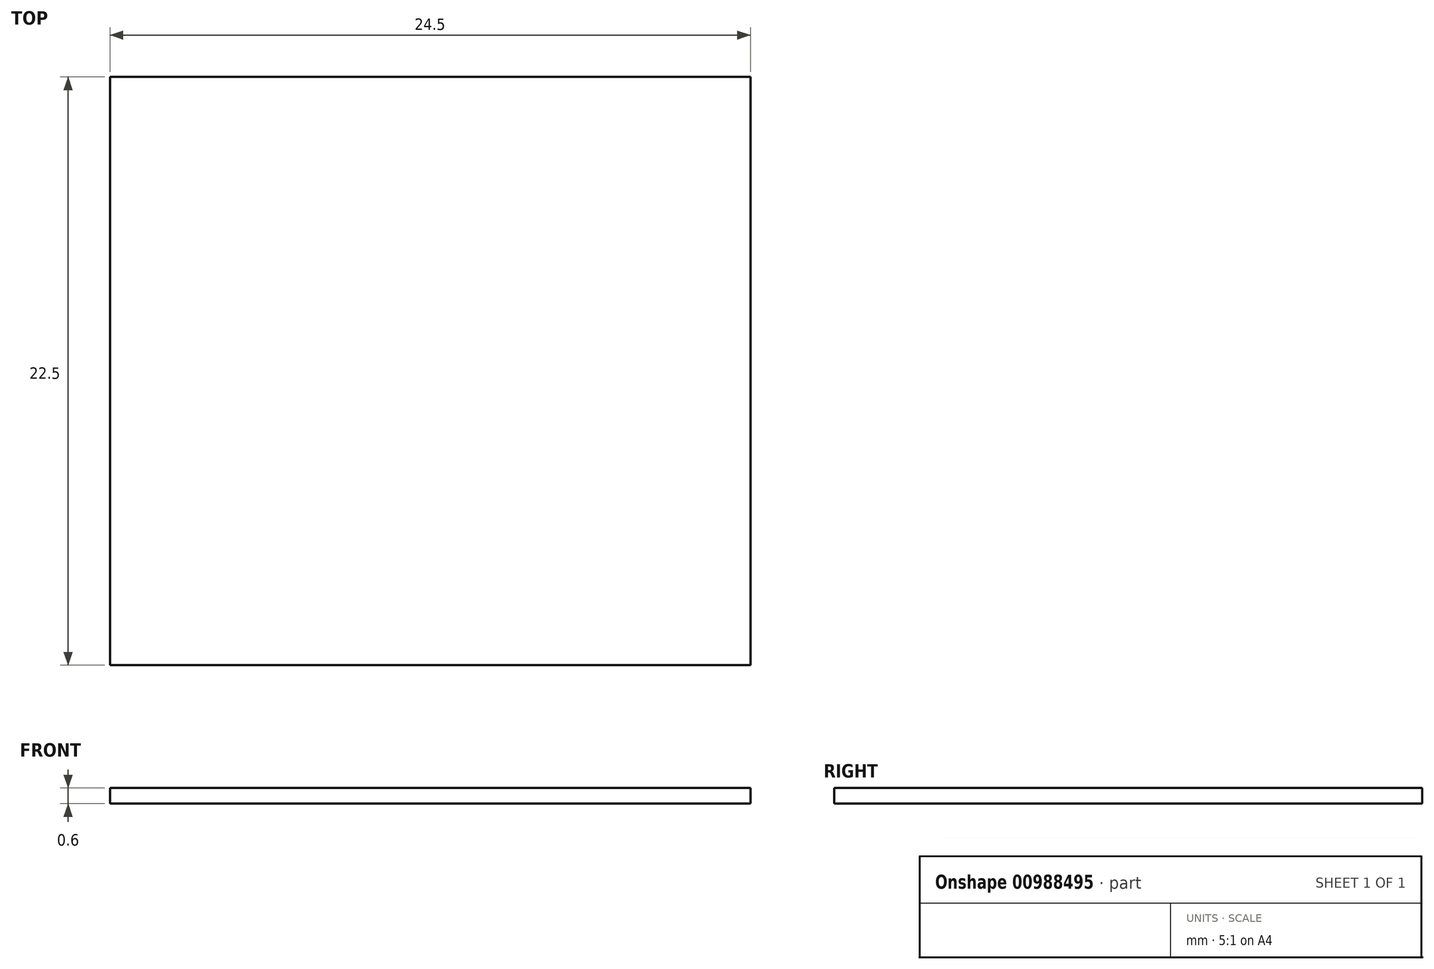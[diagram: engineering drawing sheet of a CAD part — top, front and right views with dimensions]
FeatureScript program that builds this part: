
annotation { "Feature Type Name" : "Feature", "Feature Type Description" : "" }
export const myFeature = defineFeature(function(context is Context, id is Id, definition is map)
    precondition{}
    {
        {
            var Q0;
            Q0=qCreatedBy(makeId("Top.planeOp"),FACE);
            var sketch = newSketch(context, id + "F0", { "sketchPlane" : qUnion([Q0])});
            skLineSegment(sketch, "E0.bottom", {"start": v(12.25, 11.25) * mm, "end": v(-12.25, 11.25) * mm});
            skLineSegment(sketch, "E0.top", {"start": v(12.25, -11.25) * mm, "end": v(-12.25, -11.25) * mm});
            skLineSegment(sketch, "E0.left", {"start": v(12.25, 11.25) * mm, "end": v(12.25, -11.25) * mm});
            skLineSegment(sketch, "E0.right", {"start": v(-12.25, 11.25) * mm, "end": v(-12.25, -11.25) * mm});
            skPoint(sketch, "E0.middle", {"position": v(0, 0) * mm});
            skSolve(sketch);
        }
        {
            var Q0;
            Q0=makeQuery(id+"F0.imprint","IMPRINT",FACE,{"disambiguationData":[TD([[makeQuery(id+"F0.imprint","IMPRINT",EDGE,{"derivedFrom":sQuery(id+"F0.wireOp",EDGE,"E0.bottom")}),1.0]])]});
            extrude(context, id + "F1", {"entities" : qUnion([Q0]), "oppositeDirection" : true, "depth" : .6 * mm, "offsetDistance" : 25 * mm});
        }
    });
